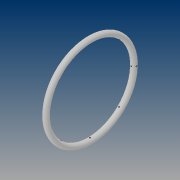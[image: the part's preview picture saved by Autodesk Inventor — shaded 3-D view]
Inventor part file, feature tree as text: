
AUTODESK INVENTOR PART (.ipt)
format: ipt  version: 2021 (Build 250183000, 183)  size: 245,760 bytes
history: native  units: mm
features: sketch x4, revolve x2, extrude x2, pattern_circular x1, plane x1
ambient origin geometry x8: Origin, YZ Plane, XZ Plane, XY Plane, X Axis, Y Axis, Z Axis, Center Point
bodies: Solid1 (feature_tree)
feature tree (10):
  revolve  "Revolution1"  [1 undecoded]
  extrude  "Extrusion1"  Depth=12.0mm
  pattern_circular  "Circular Pattern2"  Count=8 Angle=360.0deg
  plane  "Work Plane1"
  extrude  "Extrusion2"  Depth=443.684mm
  revolve  "Revolution2"  [1 undecoded]
  sketch  "Sketch1"  dims[d0=55.0mm d1=443.684mm]
  sketch  "Sketch2"  dims[d2=90.0deg d3=12.0mm]
  sketch  "Sketch4"  dims[d4=887.368mm d5=0.0mm d9=80.0mm d10=360.0deg]
  sketch  "Sketch5"  dims[d12=30.0mm d13=15.0mm d14=443.684mm d15=10.0mm d16=0.0mm d17=50.0mm d18=443.684mm d19=90.0deg]
note: 2 required parameter values undecoded (feature->parameter linkage not recoverable at this tier; creation-order binding heuristic only, values carry confidence <= 0.55)
